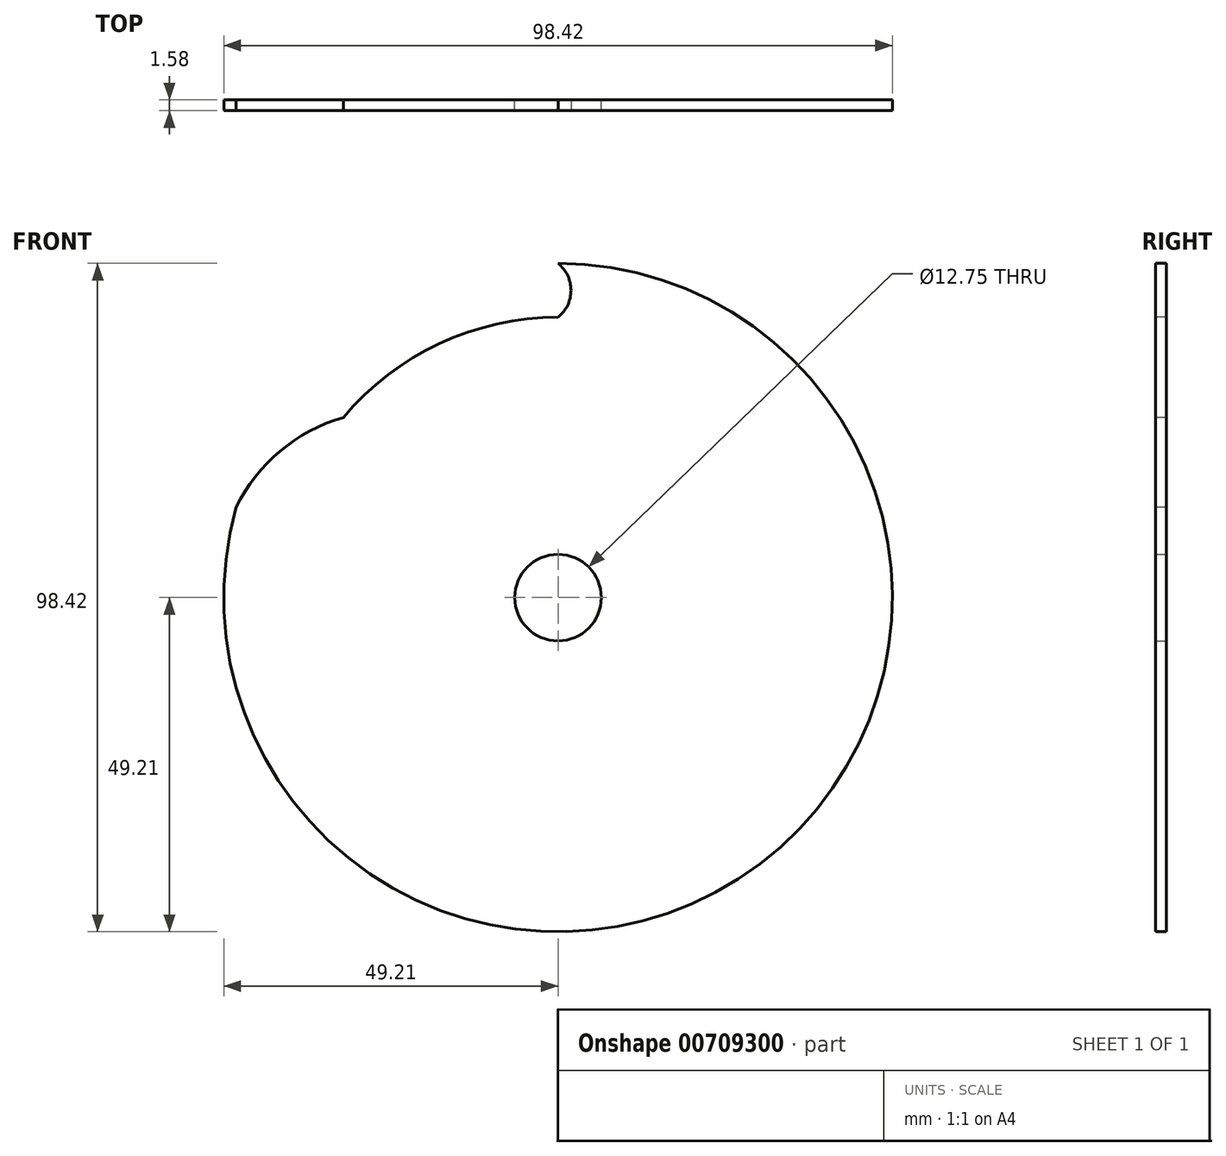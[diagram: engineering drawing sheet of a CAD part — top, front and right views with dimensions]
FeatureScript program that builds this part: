
annotation { "Feature Type Name" : "Feature", "Feature Type Description" : "" }
export const myFeature = defineFeature(function(context is Context, id is Id, definition is map)
    precondition{}
    {
        {
            var Q0;
            Q0=qCreatedBy(makeId("Front.planeOp"),FACE);
            var sketch = newSketch(context, id + "F0", { "sketchPlane" : qUnion([Q0])});
            skCircle(sketch, "E0", {"center": v(0, 0) * mm, "radius": 49.21 * mm});
            skCircle(sketch, "E1", {"center": v(0, 0) * mm, "radius": 41.28 * mm, "construction": true});
            skCircle(sketch, "E2", {"center": v(0, 0) * mm, "radius": 45.24 * mm, "construction": true});
            skLineSegment(sketch, "E3", {"start": v(0, 0) * mm, "end": v(0, 41.28) * mm, "construction": true});
            skLineSegment(sketch, "E4", {"start": v(0, 41.28) * mm, "end": v(0, 45.24) * mm, "construction": true});
            skLineSegment(sketch, "E5", {"start": v(0, 45.24) * mm, "end": v(0, 49.21) * mm, "construction": true});
            skArc(sketch, "E6", {"start": v(0, 41.28) * mm, "mid": v(1.9, 45.24) * mm, "end": v(0, 49.21) * mm, "construction": true});
            skCircle(sketch, "E7", {"center": v(0, 0) * mm, "radius": 6.38 * mm});
            skLineSegment(sketch, "E8", {"start": v(0, 0) * mm, "end": v(-41.28, 0) * mm, "construction": true});
            skLineSegment(sketch, "E9", {"start": v(0, 0) * mm, "end": v(-31.62, 26.53) * mm, "construction": true});
            skLineSegment(sketch, "E10", {"start": v(-41.28, 0) * mm, "end": v(-49.21, 0) * mm, "construction": true});
            skArc(sketch, "E11", {"start": v(-31.62, 26.53) * mm, "mid": v(-40.9, 21.58) * mm, "end": v(-47.39, 13.29) * mm, "construction": true});
            skLineSegment(sketch, "E12", {"start": v(0, 0) * mm, "end": v(-40.65, -7.17) * mm, "construction": true});
            skSolve(sketch);
        }
        {
            var Q0;
            Q0 = qSketchRegion(id + "F0", true);
            extrude(context, id + "F1", {"entities" : qUnion([Q0]), "depth" : 1.59 * mm, "offsetDistance" : 25.4 * mm, "symmetric" : true});
        }
        {
            var Q0;
            Q0=qCreatedBy(makeId("Front.planeOp"),FACE);
            var sketch = newSketch(context, id + "F2", { "sketchPlane" : qUnion([Q0])});
            skArc(sketch, "E13", {"start": v(0, 41.28) * mm, "mid": v(-17.44, 37.4) * mm, "end": v(-31.62, 26.53) * mm});
            skArc(sketch, "E14", {"start": v(0, 41.27) * mm, "mid": v(1.9, 45.24) * mm, "end": v(0, 49.21) * mm});
            skArc(sketch, "E15", {"start": v(-31.62, 26.53) * mm, "mid": v(-40.9, 21.58) * mm, "end": v(-47.39, 13.29) * mm});
            skArc(sketch, "E16", {"start": v(0, 49.21) * mm, "mid": v(-29.73, 39.22) * mm, "end": v(-47.39, 13.29) * mm});
            skSolve(sketch);
        }
        {
            var Q0;
            Q0 = qSketchRegion(id + "F2", true);
            extrude(context, id + "F3", {"entities" : qUnion([Q0]), "operationType" : NewBodyOperationType.REMOVE, "oppositeDirection" : true, "depth" : 25.4 * mm, "offsetDistance" : 25.4 * mm, "hasSecondDirection" : true, "secondDirectionOppositeDirection" : false, "secondDirectionDepth" : 25.4 * mm});
        }
    });
